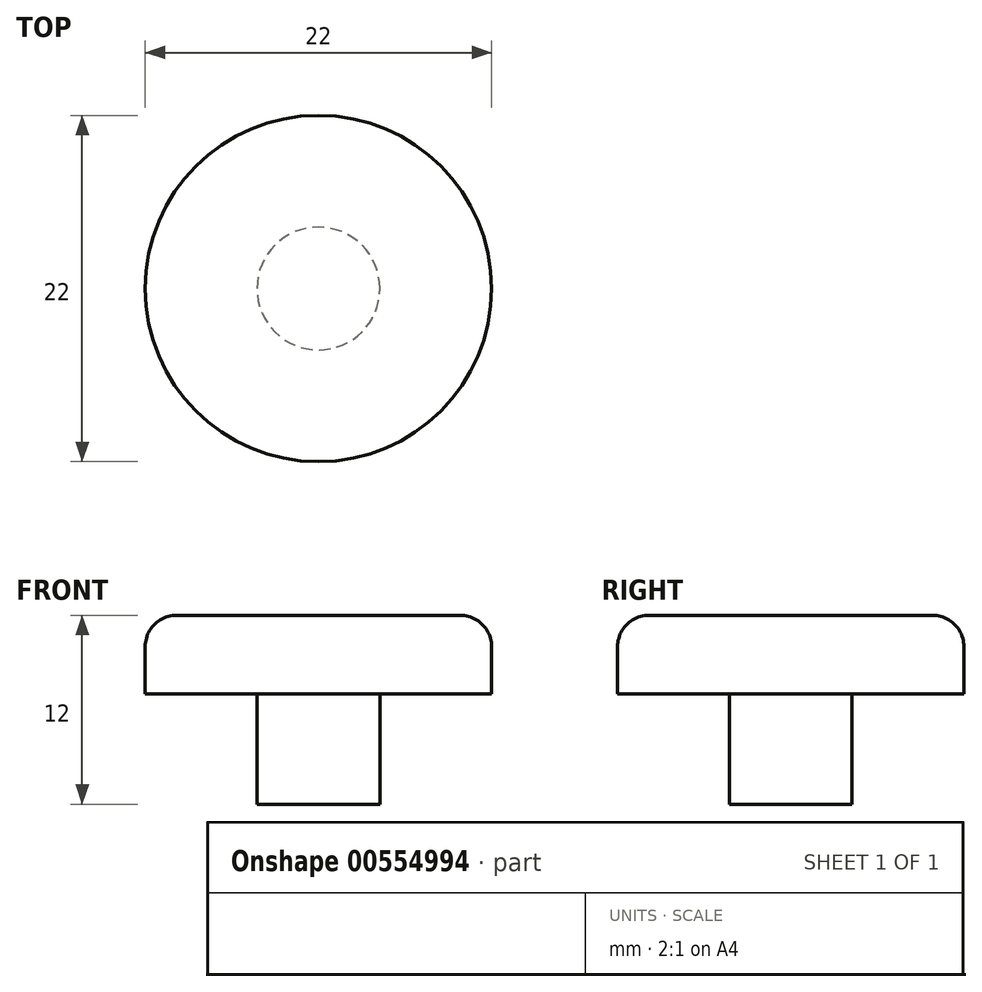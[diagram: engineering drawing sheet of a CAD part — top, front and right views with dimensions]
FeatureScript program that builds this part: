
annotation { "Feature Type Name" : "Feature", "Feature Type Description" : "" }
export const myFeature = defineFeature(function(context is Context, id is Id, definition is map)
    precondition{}
    {
        {
            var Q0;
            Q0=qCreatedBy(makeId("Top.planeOp"),FACE);
            var sketch = newSketch(context, id + "F0", { "sketchPlane" : qUnion([Q0])});
            skCircle(sketch, "E0", {"center": v(0, 0) * mm, "radius": 3.9 * mm});
            skSolve(sketch);
        }
        {
            var Q0;
            Q0 = qSketchRegion(id + "F0", true);
            extrude(context, id + "F1", {"entities" : qUnion([Q0]), "depth" : 7 * mm, "offsetDistance" : 25 * mm});
        }
        {
            var Q0;
            Q0=makeQuery(id+"F1.opExtrude","CAP_FACE",FACE,{"disambiguationData":[OSD([sQuery(id+"F0.wireOp",EDGE,"E0")])],"isStart":false});
            var sketch = newSketch(context, id + "F2", { "sketchPlane" : qUnion([Q0])});
            skCircle(sketch, "E1", {"center": v(0, 0) * mm, "radius": 11 * mm});
            skSolve(sketch);
        }
        {
            var Q0;
            Q0 = qSketchRegion(id + "F2", true);
            extrude(context, id + "F3", {"entities" : qUnion([Q0]), "operationType" : NewBodyOperationType.ADD, "depth" : 5 * mm, "offsetDistance" : 25 * mm});
        }
        {
            var Q0;
            Q0=makeQuery(id+"F3.opExtrude","CAP_FACE",FACE,{"disambiguationData":[OSD([sQuery(id+"F2.wireOp",EDGE,"E1")])],"isStart":false});
            fillet(context, id + "F4", {"entities" : qUnion([Q0]), "radius" : 2 * mm, "tangentPropagation" : true, "allowEdgeOverflow" : false});
        }
    });
